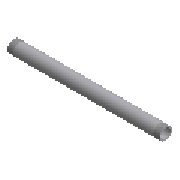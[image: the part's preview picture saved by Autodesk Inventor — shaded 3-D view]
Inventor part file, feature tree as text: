
AUTODESK INVENTOR PART (.ipt)
format: ipt  version: 2016 (Build 200138000, 138)  size: 165,376 bytes
history: native  units: mm (DEFAULTED — no unit token found)
features: other x8, revolve x1, sketch x1
ambient origin geometry x8: Origin, YZ Plane, XZ Plane, XY Plane, X Axis, Y Axis, Z Axis, Center Point
bodies: Solid1 (feature_tree)
feature tree (10):
  revolve  "Revolution1"  [1 undecoded]
  other  "Work Axis1"
  other  "Work Point5"
  other  "Work Axis2"
  other  "Work Point6"
  other  "Work Axis3"
  other  "Work Axis4"
  other  "Work Point7"
  other  "Work Point8"
  sketch  "Sketch1"  dims[d0=101.6mm d1=0.312398mm d2=92.0496mm d3=172.72mm d28=90.0deg d4=31.75mm d30=25.4mm d31=0.0mm d32=25.4mm d33=0.0mm d5=101.996748mm]
note: 1 required parameter value undecoded (feature->parameter linkage not recoverable at this tier; creation-order binding heuristic only, values carry confidence <= 0.55)
